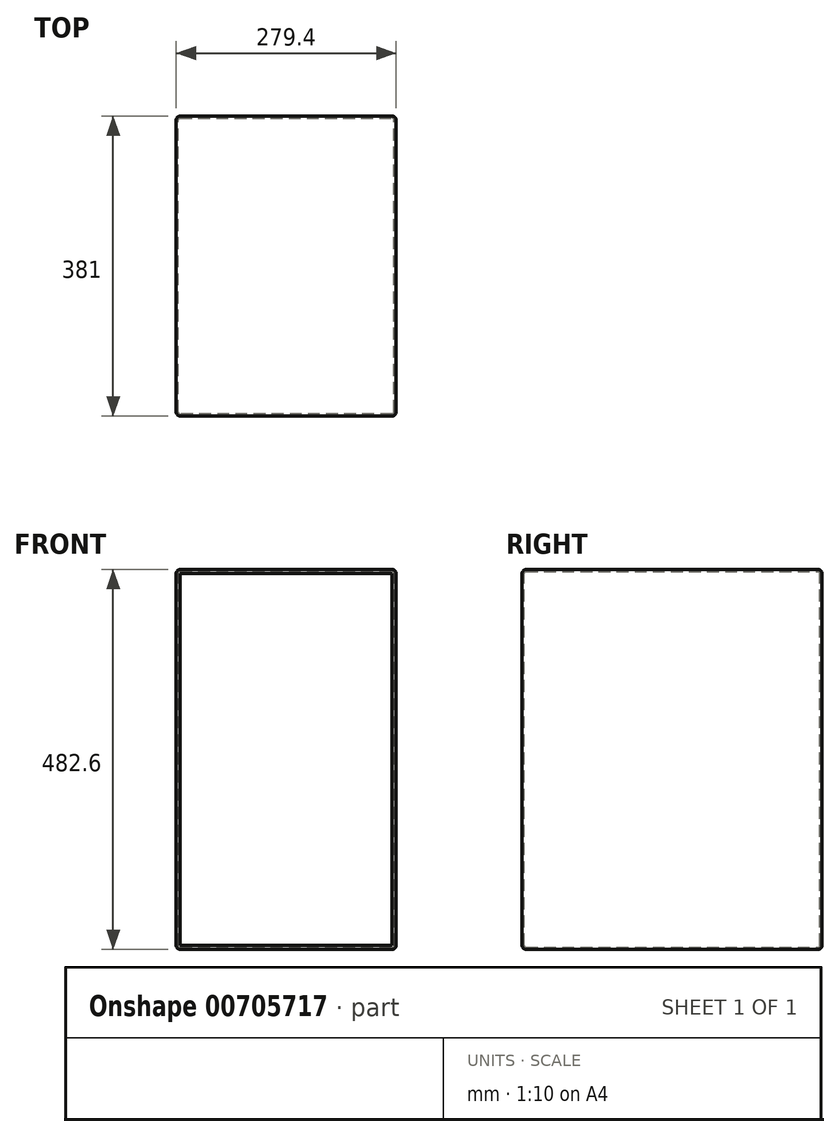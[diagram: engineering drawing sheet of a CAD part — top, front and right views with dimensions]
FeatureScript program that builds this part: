
annotation { "Feature Type Name" : "Feature", "Feature Type Description" : "" }
export const myFeature = defineFeature(function(context is Context, id is Id, definition is map)
    precondition{}
    {
        {
            var Q0;
            Q0=qCreatedBy(makeId("Front.planeOp"),FACE);
            var sketch = newSketch(context, id + "F0", { "sketchPlane" : qUnion([Q0])});
            skLineSegment(sketch, "E0.bottom", {"start": v(-139.7, -241.3) * mm, "end": v(139.7, -241.3) * mm});
            skLineSegment(sketch, "E0.top", {"start": v(-139.7, 241.3) * mm, "end": v(139.7, 241.3) * mm});
            skLineSegment(sketch, "E0.left", {"start": v(-139.7, -241.3) * mm, "end": v(-139.7, 241.3) * mm});
            skLineSegment(sketch, "E0.right", {"start": v(139.7, -241.3) * mm, "end": v(139.7, 241.3) * mm});
            skPoint(sketch, "E0.middle", {"position": v(0, 0) * mm});
            skSolve(sketch);
        }
        {
            var Q0;
            Q0=qSketchRegion(id+"F0",true);
            extrude(context, id + "F1", {"entities" : qUnion([Q0]), "depth" : 381 * mm, "offsetDistance" : 25.4 * mm});
        }
        {
            var Q0;
            Q0=makeQuery(id+"F1.opExtrude","CAP_FACE",FACE,{"disambiguationData":[OSD([sQuery(id+"F0.wireOp",EDGE,"E0.bottom"),sQuery(id+"F0.wireOp",EDGE,"E0.top"),sQuery(id+"F0.wireOp",EDGE,"E0.left"),sQuery(id+"F0.wireOp",EDGE,"E0.right")])],"isStart":false});
            fillet(context, id + "F2", {"entities" : qUnion([Q0]), "radius" : 5.08 * mm, "tangentPropagation" : true, "allowEdgeOverflow" : false});
        }
        {
            var Q0;
            Q0=makeQuery(id+"F1.opExtrude","SWEPT_FACE",FACE,{"disambiguationData":[OSD([sQuery(id+"F0.wireOp",EDGE,"E0.left")])]});
            fillet(context, id + "F3", {"entities" : qUnion([Q0]), "radius" : 5.08 * mm, "tangentPropagation" : true, "allowEdgeOverflow" : false});
        }
        {
            var Q0;
            Q0=makeQuery(id+"F1.opExtrude","CAP_FACE",FACE,{"disambiguationData":[OSD([sQuery(id+"F0.wireOp",EDGE,"E0.bottom"),sQuery(id+"F0.wireOp",EDGE,"E0.top"),sQuery(id+"F0.wireOp",EDGE,"E0.left"),sQuery(id+"F0.wireOp",EDGE,"E0.right")])],"isStart":true});
            fillet(context, id + "F4", {"entities" : qUnion([Q0]), "radius" : 5.08 * mm, "tangentPropagation" : true, "allowEdgeOverflow" : false});
        }
        {
            var Q0;
            Q0=makeQuery(id+"F1.opExtrude","SWEPT_FACE",FACE,{"disambiguationData":[OSD([sQuery(id+"F0.wireOp",EDGE,"E0.right")])]});
            fillet(context, id + "F5", {"entities" : qUnion([Q0]), "radius" : 5.08 * mm, "tangentPropagation" : true, "allowEdgeOverflow" : false});
        }
        {
            var Q0;
            Q0=makeQuery(id+"F1.opExtrude","CAP_FACE",FACE,{"disambiguationData":[OSD([sQuery(id+"F0.wireOp",EDGE,"E0.bottom"),sQuery(id+"F0.wireOp",EDGE,"E0.top"),sQuery(id+"F0.wireOp",EDGE,"E0.left"),sQuery(id+"F0.wireOp",EDGE,"E0.right")])],"isStart":false});
            shell(context, id + "F6", {"entities" : qUnion([Q0]), "thickness" : 2.54 * mm});
        }
    });
